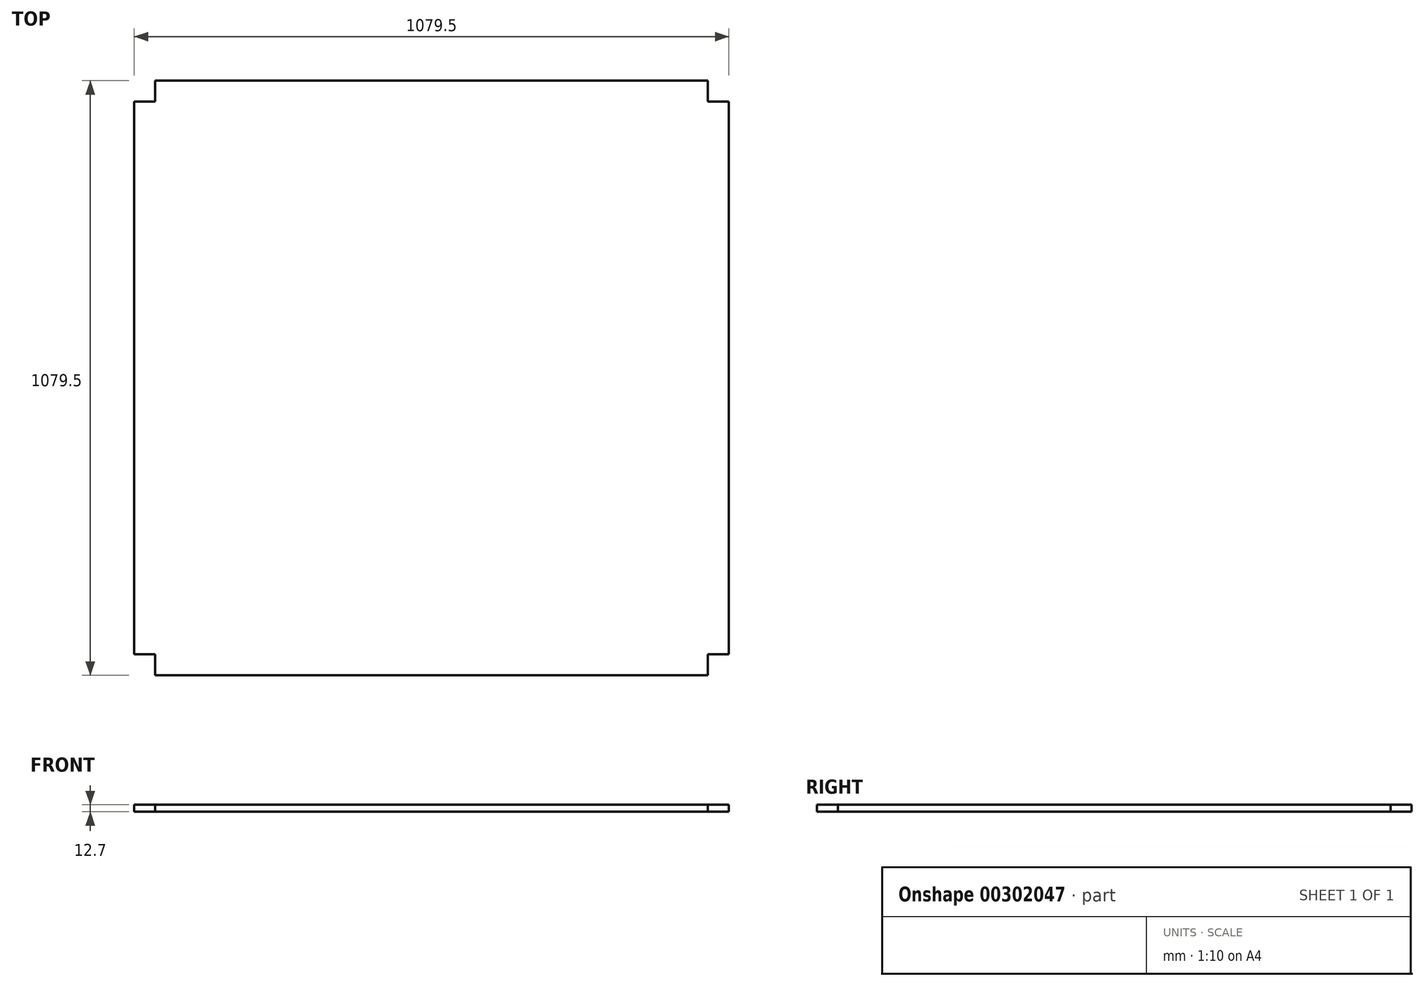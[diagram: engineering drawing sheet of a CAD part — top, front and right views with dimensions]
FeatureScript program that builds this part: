
annotation { "Feature Type Name" : "Feature", "Feature Type Description" : "" }
export const myFeature = defineFeature(function(context is Context, id is Id, definition is map)
    precondition{}
    {
        {
            var Q0;
            Q0=qCreatedBy(makeId("Top.planeOp"),FACE);
            var sketch = newSketch(context, id + "F0", { "sketchPlane" : qUnion([Q0])});
            skLineSegment(sketch, "E0", {"start": v(-520.7, 520.7) * mm, "end": v(-520.7, -482.6) * mm});
            skLineSegment(sketch, "E1", {"start": v(-520.7, -482.6) * mm, "end": v(-482.6, -482.6) * mm});
            skLineSegment(sketch, "E2", {"start": v(-482.6, -482.6) * mm, "end": v(-482.6, -520.7) * mm});
            skLineSegment(sketch, "E3", {"start": v(-482.6, -520.7) * mm, "end": v(520.7, -520.7) * mm});
            skLineSegment(sketch, "E4", {"start": v(520.7, -520.7) * mm, "end": v(520.7, -482.6) * mm});
            skLineSegment(sketch, "E5", {"start": v(520.7, -482.6) * mm, "end": v(558.8, -482.6) * mm});
            skLineSegment(sketch, "E6", {"start": v(558.8, -482.6) * mm, "end": v(558.8, 520.7) * mm});
            skLineSegment(sketch, "E7", {"start": v(558.8, 520.7) * mm, "end": v(520.7, 520.7) * mm});
            skLineSegment(sketch, "E8", {"start": v(520.7, 520.7) * mm, "end": v(520.7, 558.8) * mm});
            skLineSegment(sketch, "E9", {"start": v(520.7, 558.8) * mm, "end": v(-482.6, 558.8) * mm});
            skLineSegment(sketch, "E10", {"start": v(-482.6, 558.8) * mm, "end": v(-482.6, 520.7) * mm});
            skLineSegment(sketch, "E11", {"start": v(-482.6, 520.7) * mm, "end": v(-520.7, 520.7) * mm});
            skSolve(sketch);
        }
        {
            var Q0;
            Q0=makeQuery(id+"F0.imprint","IMPRINT",FACE,{"disambiguationData":[TD([[makeQuery(id+"F0.imprint","IMPRINT",EDGE,{"derivedFrom":sQuery(id+"F0.wireOp",EDGE,"E0")}),1.0]])]});
            extrude(context, id + "F1", {"entities" : qUnion([Q0]), "depth" : 12.7 * mm});
        }
    });
